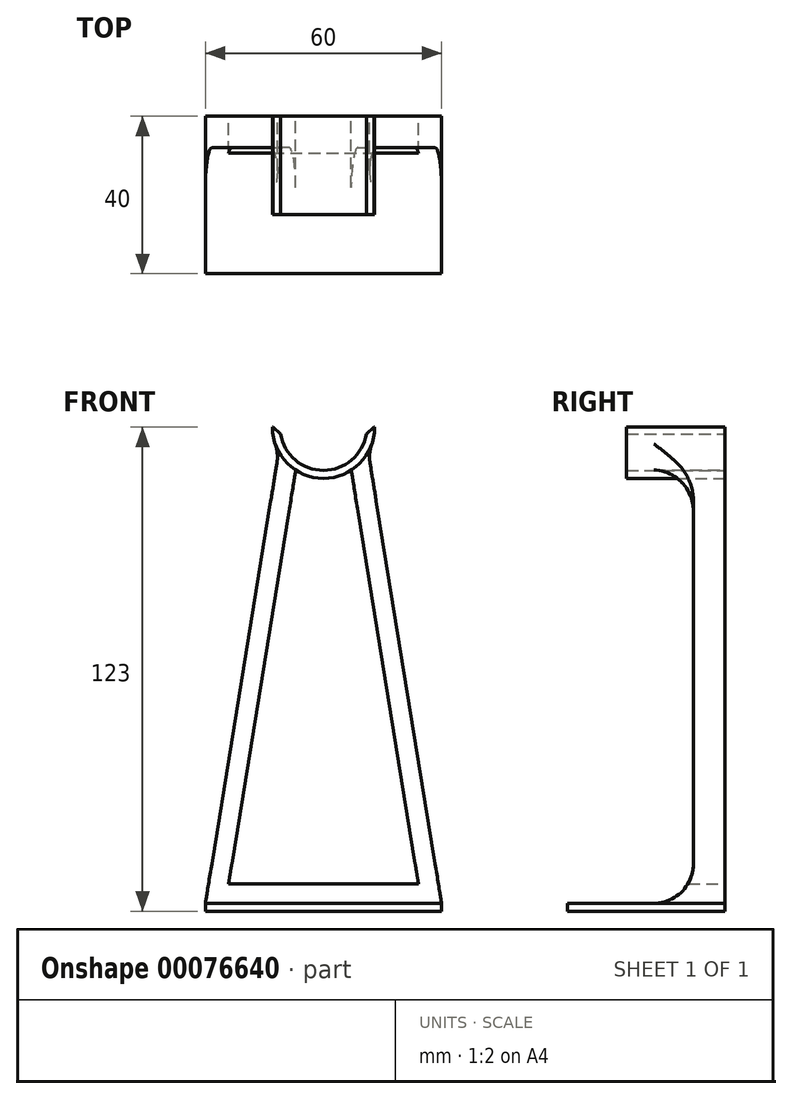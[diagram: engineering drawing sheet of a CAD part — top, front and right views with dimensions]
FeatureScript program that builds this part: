
annotation { "Feature Type Name" : "Feature", "Feature Type Description" : "" }
export const myFeature = defineFeature(function(context is Context, id is Id, definition is map)
    precondition{}
    {
        {
            var Q0;
            Q0=qCreatedBy(makeId("Front.planeOp"),FACE);
            var sketch = newSketch(context, id + "F0", { "sketchPlane" : qUnion([Q0])});
            skLineSegment(sketch, "E0", {"start": v(-22, 32.11) * mm, "end": v(0, 32.11) * mm, "construction": true});
            skArc(sketch, "E1", {"start": v(-22, 32.11) * mm, "mid": v(-11, 21.11) * mm, "end": v(0, 32.11) * mm});
            skPoint(sketch, "E2", {"position": v(-11, 21.11) * mm});
            skArc(sketch, "E3.0", {"start": v(-24, 32.11) * mm, "mid": v(-11, 19.11) * mm, "end": v(2, 32.11) * mm});
            skLineSegment(sketch, "E4", {"start": v(-24, 32.11) * mm, "end": v(-22, 32.11) * mm});
            skLineSegment(sketch, "E5", {"start": v(0, 32.11) * mm, "end": v(2, 32.11) * mm});
            skLineSegment(sketch, "E6", {"start": v(-22.37, 25.81) * mm, "end": v(-41, -88.89) * mm});
            skLineSegment(sketch, "E7", {"start": v(0.37, 25.81) * mm, "end": v(19, -88.89) * mm});
            skLineSegment(sketch, "E8", {"start": v(19, -88.89) * mm, "end": v(-41, -88.89) * mm});
            skPoint(sketch, "E9", {"position": v(-11, -88.89) * mm});
            skLineSegment(sketch, "E10", {"start": v(-11, 21.11) * mm, "end": v(-11, -88.89) * mm, "construction": true});
            skLineSegment(sketch, "E11.0", {"start": v(19, -90.89) * mm, "end": v(-41, -90.89) * mm});
            skLineSegment(sketch, "E12", {"start": v(-41, -88.89) * mm, "end": v(-41, -90.89) * mm});
            skLineSegment(sketch, "E13", {"start": v(19, -88.89) * mm, "end": v(19, -90.89) * mm});
            skLineSegment(sketch, "E14.0", {"start": v(-3.96, 21.25) * mm, "end": v(13.11, -83.88) * mm});
            skLineSegment(sketch, "E14.1", {"start": v(13.11, -83.88) * mm, "end": v(-35.11, -83.88) * mm});
            skLineSegment(sketch, "E14.2", {"start": v(-18.04, 21.23) * mm, "end": v(-35.11, -83.88) * mm});
            skPoint(sketch, "E15", {"position": v(-18.04, 21.23) * mm});
            skPoint(sketch, "E16", {"position": v(-3.96, 21.25) * mm});
            skSolve(sketch);
        }
        {
            var Q0;
            Q0=makeQuery(id+"F0.imprint","IMPRINT",FACE,{"disambiguationData":[TD([[makeQuery(id+"F0.imprint","IMPRINT",EDGE,{"derivedFrom":sQuery(id+"F0.wireOp",EDGE,"E1")}),-1.0]])]});
            var Q1;
            {var subQ1=sQuery(id+"F0.wireOp",EDGE,"E6");Q1=makeQuery(id+"F0.imprint","IMPRINT",FACE,{"disambiguationData":[TD([[makeQuery(id+"F0.imprint","IMPRINT",EDGE,{"derivedFrom":subQ1}),1.0]])]});}
            var Q2;
            Q2=makeQuery(id+"F0.imprint","IMPRINT",FACE,{"disambiguationData":[TD([[makeQuery(id+"F0.imprint","IMPRINT",EDGE,{"derivedFrom":sQuery(id+"F0.wireOp",EDGE,"E8")}),1.0]])]});
            extrude(context, id + "F1", {"entities" : qUnion([Q0, Q1, Q2]), "depth" : 8 * mm});
        }
        {
            var Q0;
            Q0=makeQuery(id+"F0.imprint","IMPRINT",FACE,{"disambiguationData":[TD([[makeQuery(id+"F0.imprint","IMPRINT",EDGE,{"derivedFrom":sQuery(id+"F0.wireOp",EDGE,"E8")}),1.0]])]});
            extrude(context, id + "F2", {"entities" : qUnion([Q0]), "operationType" : NewBodyOperationType.ADD, "depth" : 40 * mm});
        }
        {
            var Q0;
            Q0=makeQuery(id+"F0.imprint","IMPRINT",FACE,{"disambiguationData":[TD([[makeQuery(id+"F0.imprint","IMPRINT",EDGE,{"derivedFrom":sQuery(id+"F0.wireOp",EDGE,"E1")}),-1.0]])]});
            extrude(context, id + "F3", {"entities" : qUnion([Q0]), "operationType" : NewBodyOperationType.ADD, "depth" : 25 * mm});
        }
        {
            var Q0;
            {var subQ0=sQuery(id+"F0.wireOp",EDGE,"E4");var subQ1=sQuery(id+"F0.wireOp",EDGE,"E1");Q0=makeQuery(id+"F3.boolean.opBoolean","MERGE",EDGE,{"derivedFrom":[makeQuery(id+"F1.opExtrude","SWEPT_EDGE",EDGE,{"disambiguationData":[OSD([subQ1,subQ0])]}),makeQuery(id+"F3.opExtrude","SWEPT_EDGE",EDGE,{"disambiguationData":[OSD([subQ1,subQ0])]})]});}
            var Q1;
            {var subQ0=sQuery(id+"F0.wireOp",EDGE,"E5");var subQ1=sQuery(id+"F0.wireOp",EDGE,"E1");Q1=makeQuery(id+"F3.boolean.opBoolean","MERGE",EDGE,{"derivedFrom":[makeQuery(id+"F1.opExtrude","SWEPT_EDGE",EDGE,{"disambiguationData":[OSD([subQ1,subQ0])]}),makeQuery(id+"F3.opExtrude","SWEPT_EDGE",EDGE,{"disambiguationData":[OSD([subQ1,subQ0])]})]});}
            chamfer(context, id + "F4", {"entities" : qUnion([Q0, Q1]), "width" : 2 * mm, "tangentPropagation" : true});
        }
        {
            var Q0;
            {var subQ0=sQuery(id+"F0.wireOp",EDGE,"E3.0");Q0=makeQuery(id+"F3.boolean.opBoolean","INTERSECT",EDGE,{"disambiguationData":[OD(1.0)],"derivedFrom":[makeQuery(id+"F1.opExtrude","CAP_FACE",FACE,{"disambiguationData":[OSD([sQuery(id+"F0.wireOp",EDGE,"E1"),subQ0,sQuery(id+"F0.wireOp",EDGE,"E4"),sQuery(id+"F0.wireOp",EDGE,"E5"),sQuery(id+"F0.wireOp",EDGE,"E6"),sQuery(id+"F0.wireOp",EDGE,"E7"),sQuery(id+"F0.wireOp",EDGE,"E11.0"),sQuery(id+"F0.wireOp",EDGE,"E12"),sQuery(id+"F0.wireOp",EDGE,"E13"),sQuery(id+"F0.wireOp",EDGE,"E14.0"),sQuery(id+"F0.wireOp",EDGE,"E14.1"),sQuery(id+"F0.wireOp",EDGE,"E14.2")])],"isStart":false}),makeQuery(id+"F3.opExtrude","SWEPT_FACE",FACE,{"disambiguationData":[OSD([subQ0])]})]});}
            var Q1;
            Q1=makeQuery(id+"F1.opExtrude","SWEPT_EDGE",EDGE,{"disambiguationData":[OSD([sQuery(id+"F0.wireOp",EDGE,"E3.0"),sQuery(id+"F0.wireOp",EDGE,"E7")])]});
            var Q2;
            {var subQ0=sQuery(id+"F0.wireOp",EDGE,"E3.0");Q2=makeQuery(id+"F3.boolean.opBoolean","INTERSECT",EDGE,{"disambiguationData":[OD(0.0)],"derivedFrom":[makeQuery(id+"F1.opExtrude","CAP_FACE",FACE,{"disambiguationData":[OSD([sQuery(id+"F0.wireOp",EDGE,"E1"),subQ0,sQuery(id+"F0.wireOp",EDGE,"E4"),sQuery(id+"F0.wireOp",EDGE,"E5"),sQuery(id+"F0.wireOp",EDGE,"E6"),sQuery(id+"F0.wireOp",EDGE,"E7"),sQuery(id+"F0.wireOp",EDGE,"E11.0"),sQuery(id+"F0.wireOp",EDGE,"E12"),sQuery(id+"F0.wireOp",EDGE,"E13"),sQuery(id+"F0.wireOp",EDGE,"E14.0"),sQuery(id+"F0.wireOp",EDGE,"E14.1"),sQuery(id+"F0.wireOp",EDGE,"E14.2")])],"isStart":false}),makeQuery(id+"F3.opExtrude","SWEPT_FACE",FACE,{"disambiguationData":[OSD([subQ0])]})]});}
            var Q3;
            Q3=makeQuery(id+"F1.opExtrude","SWEPT_EDGE",EDGE,{"disambiguationData":[OSD([sQuery(id+"F0.wireOp",EDGE,"E3.0"),sQuery(id+"F0.wireOp",EDGE,"E6")])]});
            var Q4;
            Q4=makeQuery(id+"F2.boolean.opBoolean","INTERSECT",EDGE,{"derivedFrom":[makeQuery(id+"F1.opExtrude","CAP_FACE",FACE,{"disambiguationData":[OSD([sQuery(id+"F0.wireOp",EDGE,"E1"),sQuery(id+"F0.wireOp",EDGE,"E3.0"),sQuery(id+"F0.wireOp",EDGE,"E4"),sQuery(id+"F0.wireOp",EDGE,"E5"),sQuery(id+"F0.wireOp",EDGE,"E6"),sQuery(id+"F0.wireOp",EDGE,"E7"),sQuery(id+"F0.wireOp",EDGE,"E11.0"),sQuery(id+"F0.wireOp",EDGE,"E12"),sQuery(id+"F0.wireOp",EDGE,"E13"),sQuery(id+"F0.wireOp",EDGE,"E14.0"),sQuery(id+"F0.wireOp",EDGE,"E14.1"),sQuery(id+"F0.wireOp",EDGE,"E14.2")])],"isStart":false}),makeQuery(id+"F2.opExtrude","SWEPT_FACE",FACE,{"disambiguationData":[OSD([sQuery(id+"F0.wireOp",EDGE,"E8")])]})]});
            fillet(context, id + "F5", {"entities" : qUnion([Q0, Q1, Q2, Q3, Q4]), "radius" : 10.1 * mm, "tangentPropagation" : true, "allowEdgeOverflow" : false});
        }
    });
